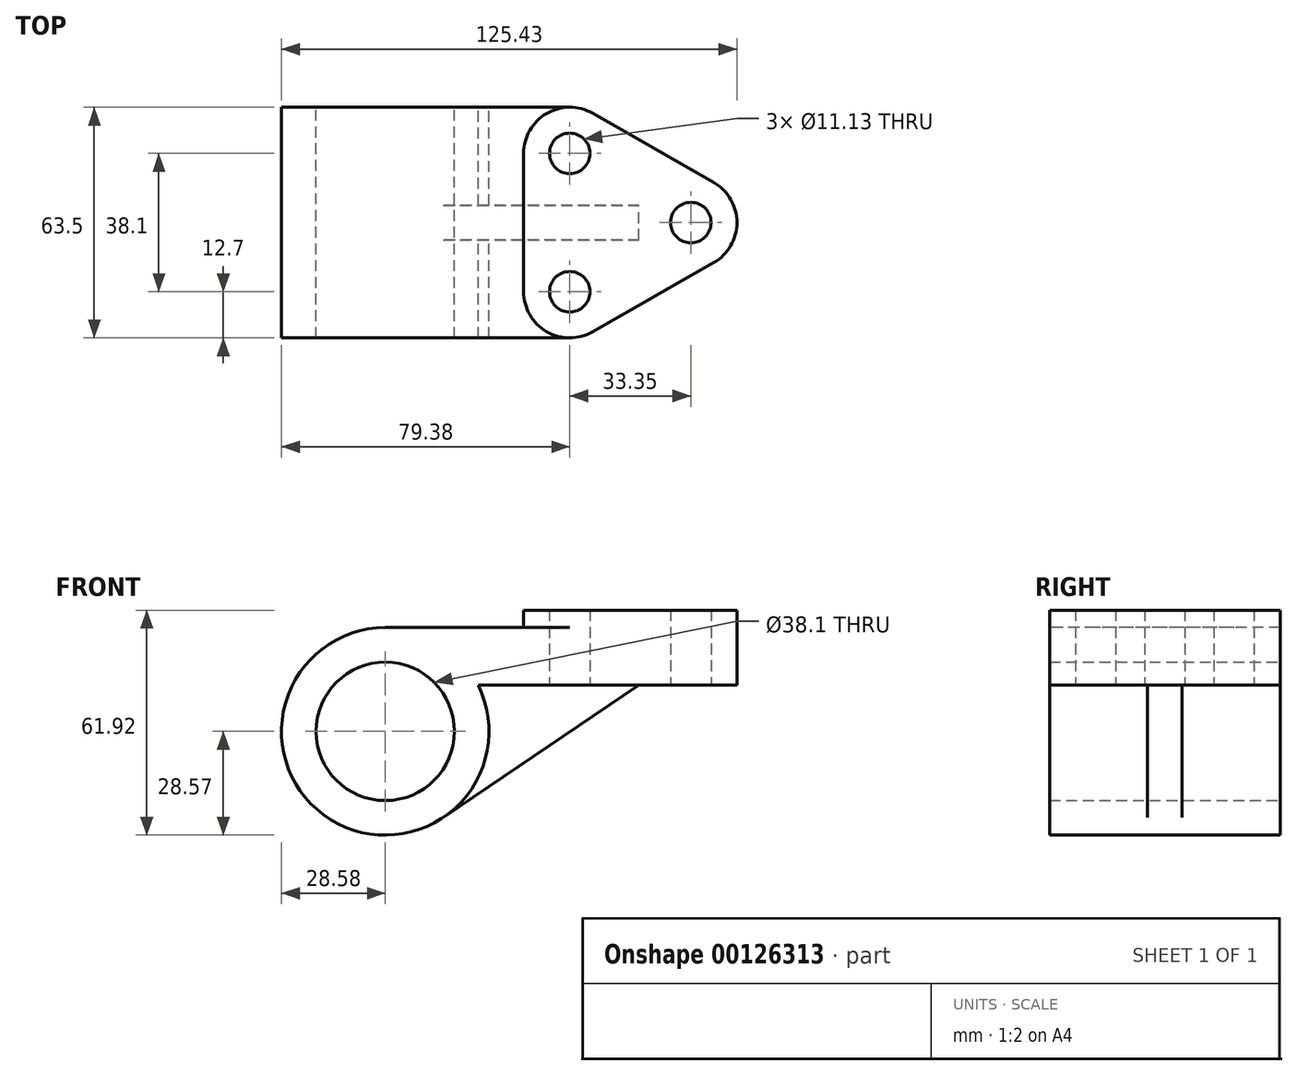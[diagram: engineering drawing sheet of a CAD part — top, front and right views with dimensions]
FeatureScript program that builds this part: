
annotation { "Feature Type Name" : "Feature", "Feature Type Description" : "" }
export const myFeature = defineFeature(function(context is Context, id is Id, definition is map)
    precondition{}
    {
        {
            var Q0;
            Q0=qCreatedBy(makeId("Top.planeOp"),FACE);
            var sketch = newSketch(context, id + "F0", { "sketchPlane" : qUnion([Q0])});
            skCircle(sketch, "E0", {"center": v(0, 0) * mm, "radius": 5.56 * mm});
            skCircle(sketch, "E1", {"center": v(0, 0) * mm, "radius": 12.7 * mm});
            skLineSegment(sketch, "E2", {"start": v(0, 0) * mm, "end": v(-33.35, 0) * mm, "construction": true});
            skLineSegment(sketch, "E3", {"start": v(-33.35, 0) * mm, "end": v(-33.35, 19.05) * mm, "construction": true});
            skLineSegment(sketch, "E4", {"start": v(-33.35, 0) * mm, "end": v(-33.35, -19.05) * mm, "construction": true});
            skCircle(sketch, "E5", {"center": v(-33.35, 19.05) * mm, "radius": 5.56 * mm});
            skCircle(sketch, "E6", {"center": v(-33.35, -19.05) * mm, "radius": 5.56 * mm});
            skCircle(sketch, "E7", {"center": v(-33.35, 19.05) * mm, "radius": 12.7 * mm});
            skCircle(sketch, "E8", {"center": v(-33.35, -19.05) * mm, "radius": 12.7 * mm});
            skLineSegment(sketch, "E9", {"start": v(6.3, 11.03) * mm, "end": v(-27.05, 30.08) * mm});
            skLineSegment(sketch, "E10", {"start": v(-27.05, -30.08) * mm, "end": v(6.3, -11.03) * mm});
            skLineSegment(sketch, "E11", {"start": v(-46.05, 19.05) * mm, "end": v(-46.05, -19.05) * mm});
            skLineSegment(sketch, "E12", {"start": v(-33.35, 31.75) * mm, "end": v(-84.15, 31.75) * mm});
            skLineSegment(sketch, "E13", {"start": v(-84.15, 31.75) * mm, "end": v(-84.15, -31.75) * mm});
            skLineSegment(sketch, "E14", {"start": v(-84.15, -31.75) * mm, "end": v(-33.35, -31.75) * mm});
            skSolve(sketch);
        }
        {
            var Q0;
            {var subQ0=sQuery(id+"F0.wireOp",EDGE,"E9");Q0=makeQuery(id+"F0.imprint","IMPRINT",FACE,{"disambiguationData":[TD([[makeQuery(id+"F0.imprint","IMPRINT",EDGE,{"derivedFrom":subQ0}),1.0]])]});}
            var Q1;
            Q1=makeQuery(id+"F0.imprint","IMPRINT",FACE,{"disambiguationData":[TD([[makeQuery(id+"F0.imprint","IMPRINT",EDGE,{"derivedFrom":sQuery(id+"F0.wireOp",EDGE,"E5")}),-1.0]])]});
            var Q2;
            Q2=makeQuery(id+"F0.imprint","IMPRINT",FACE,{"disambiguationData":[TD([[makeQuery(id+"F0.imprint","IMPRINT",EDGE,{"derivedFrom":sQuery(id+"F0.wireOp",EDGE,"E0")}),-1.0]])]});
            var Q3;
            Q3=makeQuery(id+"F0.imprint","IMPRINT",FACE,{"disambiguationData":[TD([[makeQuery(id+"F0.imprint","IMPRINT",EDGE,{"derivedFrom":sQuery(id+"F0.wireOp",EDGE,"E6")}),-1.0]])]});
            extrude(context, id + "F1", {"entities" : qUnion([Q0, Q1, Q2, Q3]), "depth" : 20.65 * mm});
        }
        {
            var Q0;
            {var subQ1=sQuery(id+"F0.wireOp",EDGE,"E11");Q0=makeQuery(id+"F0.imprint","IMPRINT",FACE,{"disambiguationData":[TD([[makeQuery(id+"F0.imprint","IMPRINT",EDGE,{"derivedFrom":subQ1}),-1.0]])]});}
            extrude(context, id + "F2", {"entities" : qUnion([Q0]), "operationType" : NewBodyOperationType.ADD, "depth" : 15.88 * mm});
        }
        {
            var Q0;
            Q0=qCreatedBy(makeId("Front.planeOp"),FACE);
            var sketch = newSketch(context, id + "F3", { "sketchPlane" : qUnion([Q0])});
            skLineSegment(sketch, "E15.0.0", {"start": v(-84.15, 0) * mm, "end": v(-33.35, 0) * mm});
            skLineSegment(sketch, "E15.0.1", {"start": v(-33.35, 0) * mm, "end": v(-33.35, 15.88) * mm});
            skLineSegment(sketch, "E15.0.2", {"start": v(-33.35, 15.88) * mm, "end": v(-84.15, 15.88) * mm});
            skLineSegment(sketch, "E15.0.3", {"start": v(-84.15, 15.88) * mm, "end": v(-84.15, 0) * mm});
            skLineSegment(sketch, "E16", {"start": v(-84.15, 15.88) * mm, "end": v(-84.15, -12.7) * mm, "construction": true});
            skCircle(sketch, "E17", {"center": v(-84.15, -12.7) * mm, "radius": 28.58 * mm});
            skCircle(sketch, "E18", {"center": v(-84.15, -12.7) * mm, "radius": 19.05 * mm});
            skArc(sketch, "E19", {"start": v(-46.18, 0) * mm, "mid": v(-53.2, -3.08) * mm, "end": v(-55.67, -10.32) * mm});
            skSolve(sketch);
        }
        {
            var Q0;
            {var subQ4=sQuery(id+"F3.wireOp",EDGE,"E15.0.0");var subQ6=sQuery(id+"F3.wireOp",EDGE,"E18");var subQ8=makeQuery(id+"F3.imprint","INTERSECT",VERTEX,{"derivedFrom":[subQ4,subQ6]});Q0=makeQuery(id+"F3.imprint","IMPRINT",FACE,{"disambiguationData":[TD([[makeQuery(id+"F3.imprint","IMPRINT",EDGE,{"disambiguationData":[TD([[subQ8,-1.0]])],"derivedFrom":subQ4}),-1.0]])]});}
            extrude(context, id + "F4", {"entities" : qUnion([Q0]), "operationType" : NewBodyOperationType.ADD, "endBound" : BoundingType.SYMMETRIC, "depth" : 63.5 * mm});
        }
        {
            var Q0;
            Q0=qCreatedBy(makeId("Front.planeOp"),FACE);
            var sketch = newSketch(context, id + "F5", { "sketchPlane" : qUnion([Q0])});
            skArc(sketch, "E20.0", {"start": v(-84.15, 6.35) * mm, "mid": v(-91.93, -30.1) * mm, "end": v(-69.95, 0) * mm});
            skLineSegment(sketch, "E21", {"start": v(-84.15, -12.7) * mm, "end": v(-84.15, 0) * mm, "construction": true});
            skLineSegment(sketch, "E22", {"start": v(-84.15, 0) * mm, "end": v(-14.3, 0) * mm, "construction": true});
            skArc(sketch, "E23.0", {"start": v(-84.15, 15.88) * mm, "mid": v(-99.21, -36.98) * mm, "end": v(-58.55, 0) * mm});
            skLineSegment(sketch, "E24", {"start": v(-14.3, 0) * mm, "end": v(-68.16, -36.38) * mm});
            skArc(sketch, "E25", {"start": v(-68.16, -36.38) * mm, "mid": v(-56.52, -20) * mm, "end": v(-58.55, 0) * mm});
            skLineSegment(sketch, "E26", {"start": v(-58.55, 0) * mm, "end": v(-14.3, 0) * mm});
            skSolve(sketch);
        }
        {
            var Q0;
            Q0=makeQuery(id+"F5.imprint","IMPRINT",FACE,{"disambiguationData":[TD([[makeQuery(id+"F5.imprint","IMPRINT",EDGE,{"derivedFrom":sQuery(id+"F5.wireOp",EDGE,"E24")}),-1.0]])]});
            extrude(context, id + "F6", {"entities" : qUnion([Q0]), "operationType" : NewBodyOperationType.ADD, "endBound" : BoundingType.SYMMETRIC, "depth" : 9.52 * mm});
        }
        {
            var Q0;
            Q0=makeQuery(id+"F4.boolean.opBoolean","MERGE",FACE,{"derivedFrom":[makeQuery(id+"F2.opExtrude","SWEPT_FACE",FACE,{"disambiguationData":[OSD([sQuery(id+"F0.wireOp",EDGE,"E14")])]}),makeQuery(id+"F4.opExtrude","CAP_FACE",FACE,{"disambiguationData":[OSD([sQuery(id+"F3.wireOp",EDGE,"E15.0.0"),sQuery(id+"F3.wireOp",EDGE,"E15.0.3"),sQuery(id+"F3.wireOp",EDGE,"E17"),sQuery(id+"F3.wireOp",EDGE,"E18")])],"isStart":false})]});
            var sketch = newSketch(context, id + "F7", { "sketchPlane" : qUnion([Q0])});
            skArc(sketch, "E27.0", {"start": v(-84.15, 6.35) * mm, "mid": v(-91.93, -30.1) * mm, "end": v(-69.95, 0) * mm});
            skCircle(sketch, "E28", {"center": v(-84.15, -12.7) * mm, "radius": 19.05 * mm});
            skSolve(sketch);
        }
        {
            var Q0;
            Q0 = qSketchRegion(id + "F7", true);
            extrude(context, id + "F8", {"entities" : qUnion([Q0]), "operationType" : NewBodyOperationType.REMOVE, "endBound" : BoundingType.SYMMETRIC, "depth" : 762 * mm});
        }
    });
